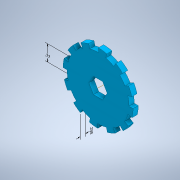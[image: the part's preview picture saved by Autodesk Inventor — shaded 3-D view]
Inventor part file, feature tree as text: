
AUTODESK INVENTOR PART (.ipt)
format: ipt  version: 2022.2 (Build 262287000, 287)  size: 949,248 bytes
history: native  units: in
note: dims shown in document units (in); Inventor stores cm internally (conversion verified against a paired STEP export)
features: sketch x4, other x3, extrude x3, pattern_circular x1, emboss x1
ambient origin geometry x8: Origin, YZ Plane, XZ Plane, XY Plane, X Axis, Y Axis, Z Axis, Center Point
bodies: Solid1 (feature_tree)
feature tree (12):
  other  "Annotations"
  extrude  "Extrusion1"  Depth=0.25in TaperAngle=0.0deg
  extrude  "Extrusion11"  TaperAngle=0.0deg  [1 undecoded]
  extrude  "Extrusion19"  Depth=0.0034in
  pattern_circular  "Circular Pattern11"  [2 undecoded]
  emboss  "Emboss1"
  sketch  "Sketch1"  dims[d0=2.985in d1=0.25in d2=0.0in]
  sketch  "Sketch10"  dims[d55=0.765in d56=0.0in d57=0.0in]
  sketch  "Sketch17"  dims[d123=0.1963in d124=0.0034in]
  sketch  "Sketch35"  dims[d125=0.0962in d126=0.25in d127=0.0in d128=4.7244in d129=360.0deg d131=2.985in d132=3.3777in d212=2.25in d213=0.1in d214=0.0in d136=0.25in d209=0.2158in d210=0.2107in d211=0.765in]
  other  "Linear Dimension 2"
  other  "Linear Dimension 3"
note: 3 required parameter values undecoded (feature->parameter linkage not recoverable at this tier; creation-order binding heuristic only, values carry confidence <= 0.55)
